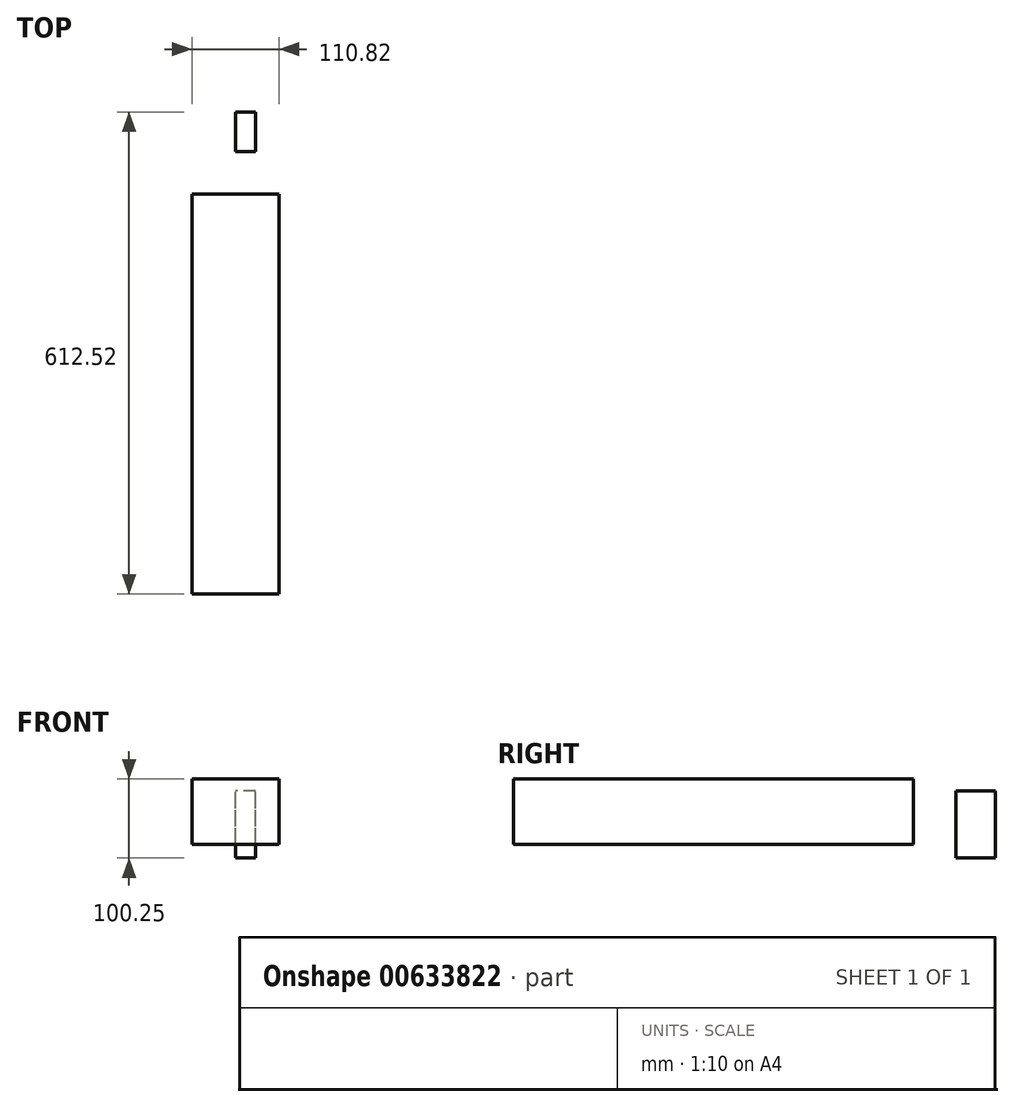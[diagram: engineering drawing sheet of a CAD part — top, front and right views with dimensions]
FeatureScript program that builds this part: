
annotation { "Feature Type Name" : "Feature", "Feature Type Description" : "" }
export const myFeature = defineFeature(function(context is Context, id is Id, definition is map)
    precondition{}
    {
        {
            var Q0;
            Q0=qCreatedBy(makeId("Front.planeOp"),FACE);
            var sketch = newSketch(context, id + "F0", { "sketchPlane" : qUnion([Q0])});
            skLineSegment(sketch, "E0.bottom", {"start": v(-55.4, 57.65) * mm, "end": v(55.4, 57.65) * mm});
            skLineSegment(sketch, "E0.top", {"start": v(-55.4, -25.44) * mm, "end": v(55.4, -25.44) * mm});
            skLineSegment(sketch, "E0.left", {"start": v(-55.4, 57.65) * mm, "end": v(-55.4, -25.44) * mm});
            skLineSegment(sketch, "E0.right", {"start": v(55.4, 57.65) * mm, "end": v(55.4, -25.44) * mm});
            skPoint(sketch, "E0.middle", {"position": v(0, 16.1) * mm});
            skSolve(sketch);
        }
        {
            var Q0;
            Q0 = qSketchRegion(id + "F0", true);
            var Q1;
            Q1=sQuery(id+"F0.wireOp",EDGE,"E0.bottom");
            var Q2;
            Q2=sQuery(id+"F0.wireOp",EDGE,"E0.left");
            extrude(context, id + "F1", {"entities" : qUnion([Q0]), "surfaceEntities" : qUnion([Q1, Q2]), "depth" : 508 * mm, "offsetDistance" : 25.4 * mm});
        }
        {
            var Q0;
            Q0=qCreatedBy(makeId("Right.planeOp"),FACE);
            var sketch = newSketch(context, id + "F2", { "sketchPlane" : qUnion([Q0])});
            skLineSegment(sketch, "E1.bottom", {"start": v(104.52, -42.6) * mm, "end": v(54.44, -42.6) * mm});
            skLineSegment(sketch, "E1.top", {"start": v(104.52, 42.6) * mm, "end": v(54.44, 42.6) * mm});
            skLineSegment(sketch, "E1.left", {"start": v(104.52, -42.6) * mm, "end": v(104.52, 42.6) * mm});
            skLineSegment(sketch, "E1.right", {"start": v(54.44, -42.6) * mm, "end": v(54.44, 42.6) * mm});
            skPoint(sketch, "E1.middle", {"position": v(79.48, 0) * mm});
            skSolve(sketch);
        }
        {
            var Q0;
            Q0 = qSketchRegion(id + "F2", true);
            extrude(context, id + "F3", {"entities" : qUnion([Q0]), "depth" : 25.4 * mm, "offsetDistance" : 25.4 * mm});
        }
    });
